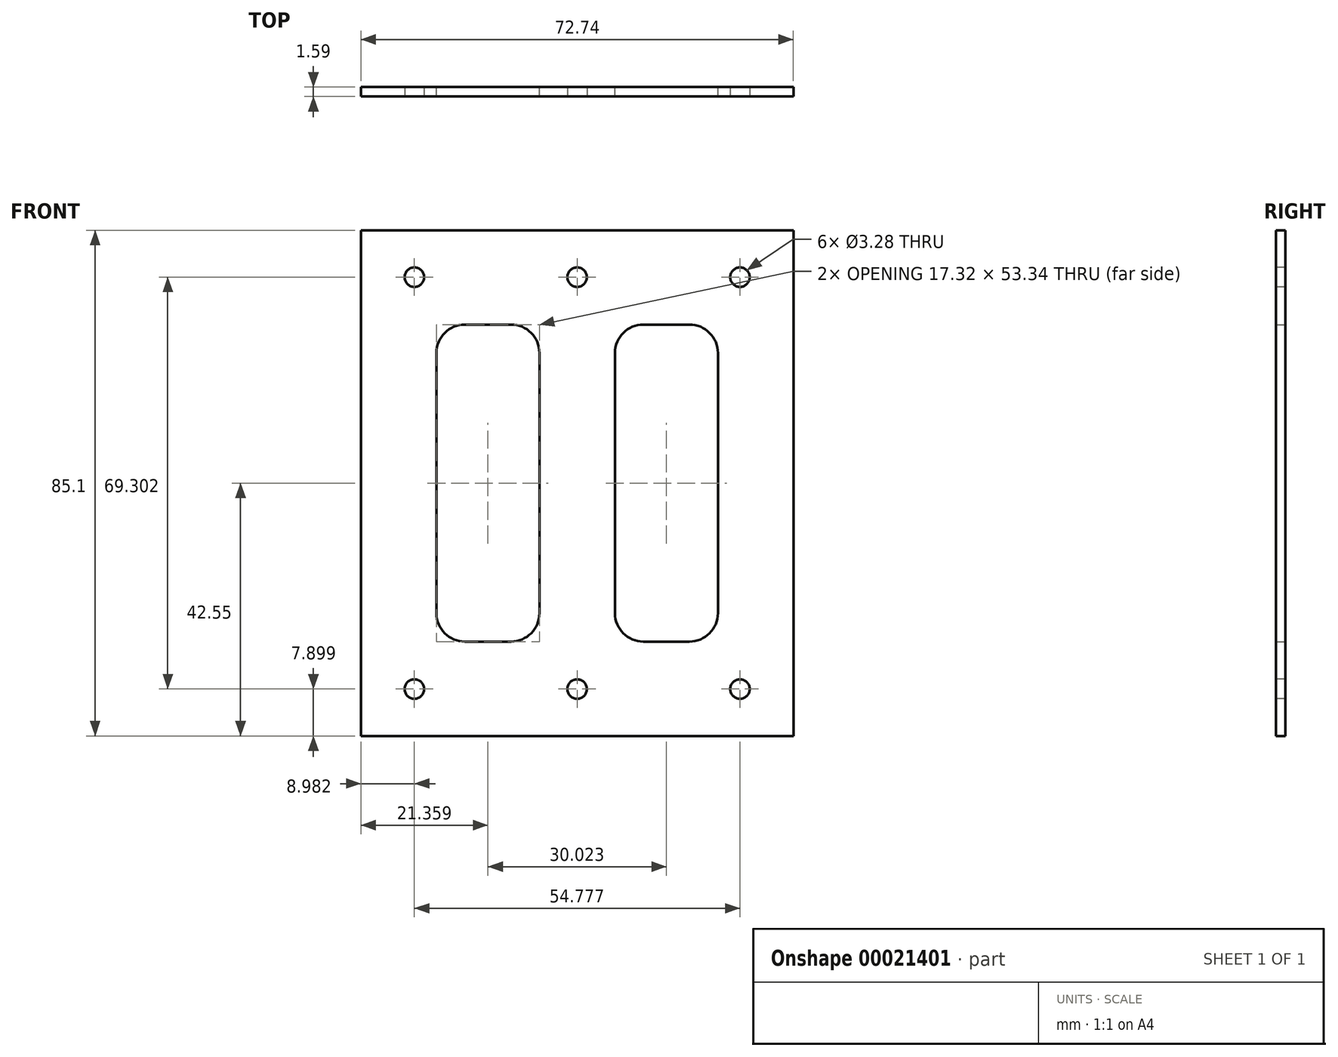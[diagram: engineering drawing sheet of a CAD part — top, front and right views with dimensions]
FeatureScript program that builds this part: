
annotation { "Feature Type Name" : "Feature", "Feature Type Description" : "" }
export const myFeature = defineFeature(function(context is Context, id is Id, definition is map)
    precondition{}
    {
        {
            var Q0;
            Q0=qCreatedBy(makeId("Front.planeOp"),FACE);
            var sketch = newSketch(context, id + "F0", { "sketchPlane" : qUnion([Q0])});
            skLineSegment(sketch, "E0.rect.bottom", {"start": v(36.37, 42.55) * mm, "end": v(-36.37, 42.55) * mm});
            skLineSegment(sketch, "E0.rect.top", {"start": v(36.37, -42.55) * mm, "end": v(-36.37, -42.55) * mm});
            skLineSegment(sketch, "E0.rect.left", {"start": v(36.37, 42.55) * mm, "end": v(36.37, -42.55) * mm});
            skLineSegment(sketch, "E0.rect.right", {"start": v(-36.37, 42.55) * mm, "end": v(-36.37, -42.55) * mm});
            skPoint(sketch, "E0.rect.middle", {"position": v(0, 0) * mm});
            skLineSegment(sketch, "E1.bottom", {"start": v(-23.67, 26.67) * mm, "end": v(-6.35, 26.67) * mm});
            skLineSegment(sketch, "E1.top", {"start": v(-23.67, -26.67) * mm, "end": v(-6.35, -26.67) * mm});
            skLineSegment(sketch, "E1.left", {"start": v(-23.67, 26.67) * mm, "end": v(-23.67, -26.67) * mm});
            skLineSegment(sketch, "E1.right", {"start": v(-6.35, 26.67) * mm, "end": v(-6.35, -26.67) * mm});
            skLineSegment(sketch, "E2.bottom", {"start": v(6.35, -26.67) * mm, "end": v(23.67, -26.67) * mm});
            skLineSegment(sketch, "E2.top", {"start": v(6.35, 26.67) * mm, "end": v(23.67, 26.67) * mm});
            skLineSegment(sketch, "E2.left", {"start": v(6.35, -26.67) * mm, "end": v(6.35, 26.67) * mm});
            skLineSegment(sketch, "E2.right", {"start": v(23.67, -26.67) * mm, "end": v(23.67, 26.67) * mm});
            skLineSegment(sketch, "E3", {"start": v(0, 0) * mm, "end": v(0, 47.22) * mm});
            skLineSegment(sketch, "E4", {"start": v(0, 0) * mm, "end": v(48.26, 0) * mm});
            skSolve(sketch);
        }
        {
            var Q0;
            {var subQ13=sQuery(id+"F0.wireOp",EDGE,"E0.rect.top");Q0=makeQuery(id+"F0.imprint","IMPRINT",FACE,{"disambiguationData":[TD([[makeQuery(id+"F0.imprint","IMPRINT",EDGE,{"derivedFrom":subQ13}),-1.0]])]});}
            var Q1;
            {var subQ9=sQuery(id+"F0.wireOp",EDGE,"E2.top");Q1=makeQuery(id+"F0.imprint","IMPRINT",FACE,{"disambiguationData":[TD([[makeQuery(id+"F0.imprint","IMPRINT",EDGE,{"derivedFrom":subQ9}),1.0]])]});}
            extrude(context, id + "F1", {"entities" : qUnion([Q0, Q1]), "depth" : 1.59 * mm});
        }
        {
            var Q0;
            Q0=makeQuery(id+"F1.opExtrude","SWEPT_EDGE",EDGE,{"disambiguationData":[OSD([sQuery(id+"F0.wireOp",EDGE,"E2.top"),sQuery(id+"F0.wireOp",EDGE,"E2.right")])]});
            var Q1;
            Q1=makeQuery(id+"F1.opExtrude","SWEPT_EDGE",EDGE,{"disambiguationData":[OSD([sQuery(id+"F0.wireOp",EDGE,"E2.top"),sQuery(id+"F0.wireOp",EDGE,"E2.left")])]});
            var Q2;
            Q2=makeQuery(id+"F1.opExtrude","SWEPT_EDGE",EDGE,{"disambiguationData":[OSD([sQuery(id+"F0.wireOp",EDGE,"E2.bottom"),sQuery(id+"F0.wireOp",EDGE,"E2.left")])]});
            var Q3;
            Q3=makeQuery(id+"F1.opExtrude","SWEPT_EDGE",EDGE,{"disambiguationData":[OSD([sQuery(id+"F0.wireOp",EDGE,"E1.top"),sQuery(id+"F0.wireOp",EDGE,"E1.left")])]});
            var Q4;
            Q4=makeQuery(id+"F1.opExtrude","SWEPT_EDGE",EDGE,{"disambiguationData":[OSD([sQuery(id+"F0.wireOp",EDGE,"E1.top"),sQuery(id+"F0.wireOp",EDGE,"E1.right")])]});
            var Q5;
            Q5=makeQuery(id+"F1.opExtrude","SWEPT_EDGE",EDGE,{"disambiguationData":[OSD([sQuery(id+"F0.wireOp",EDGE,"E1.bottom"),sQuery(id+"F0.wireOp",EDGE,"E1.left")])]});
            var Q6;
            Q6=makeQuery(id+"F1.opExtrude","SWEPT_EDGE",EDGE,{"disambiguationData":[OSD([sQuery(id+"F0.wireOp",EDGE,"E1.bottom"),sQuery(id+"F0.wireOp",EDGE,"E1.right")])]});
            var Q7;
            Q7=makeQuery(id+"F1.opExtrude","SWEPT_EDGE",EDGE,{"disambiguationData":[OSD([sQuery(id+"F0.wireOp",EDGE,"E2.bottom"),sQuery(id+"F0.wireOp",EDGE,"E2.right")])]});
            fillet(context, id + "F2", {"entities" : qUnion([Q0, Q1, Q2, Q3, Q4, Q5, Q6, Q7]), "radius" : 4.78 * mm, "tangentPropagation" : true, "allowEdgeOverflow" : false});
        }
        {
            var Q0;
            Q0=makeQuery(id+"F1.opExtrude","CAP_FACE",FACE,{"disambiguationData":[OSD([sQuery(id+"F0.wireOp",EDGE,"E0.rect.bottom"),sQuery(id+"F0.wireOp",EDGE,"E0.rect.top"),sQuery(id+"F0.wireOp",EDGE,"E0.rect.left"),sQuery(id+"F0.wireOp",EDGE,"E0.rect.right"),sQuery(id+"F0.wireOp",EDGE,"E1.bottom"),sQuery(id+"F0.wireOp",EDGE,"E1.top"),sQuery(id+"F0.wireOp",EDGE,"E1.left"),sQuery(id+"F0.wireOp",EDGE,"E1.right"),sQuery(id+"F0.wireOp",EDGE,"E2.bottom"),sQuery(id+"F0.wireOp",EDGE,"E2.top"),sQuery(id+"F0.wireOp",EDGE,"E2.left"),sQuery(id+"F0.wireOp",EDGE,"E2.right")])],"isStart":false});
            var sketch = newSketch(context, id + "F3", { "sketchPlane" : qUnion([Q0])});
            skLineSegment(sketch, "E5.rect.bottom", {"start": v(27.39, -34.65) * mm, "end": v(-27.39, -34.65) * mm});
            skLineSegment(sketch, "E5.rect.top", {"start": v(27.39, 34.65) * mm, "end": v(-27.39, 34.65) * mm});
            skLineSegment(sketch, "E5.rect.left", {"start": v(27.39, -34.65) * mm, "end": v(27.39, 34.65) * mm});
            skLineSegment(sketch, "E5.rect.right", {"start": v(-27.39, -34.65) * mm, "end": v(-27.39, 34.65) * mm});
            skPoint(sketch, "E5.rect.middle", {"position": v(0, 0) * mm});
            skLineSegment(sketch, "E6", {"start": v(0, 34.65) * mm, "end": v(0, -34.65) * mm});
            skSolve(sketch);
        }
        {
            var Q0;
            Q0=sQuery(id+"F3.wireOp",VERTEX,"E5.rect.right.end");
            var Q1;
            Q1=sQuery(id+"F3.wireOp",VERTEX,"E6.start");
            var Q2;
            Q2=sQuery(id+"F3.wireOp",VERTEX,"E5.rect.left.end");
            var Q3;
            Q3=sQuery(id+"F3.wireOp",VERTEX,"E5.rect.right.start");
            var Q4;
            Q4=sQuery(id+"F3.wireOp",VERTEX,"E6.end");
            var Q5;
            Q5=sQuery(id+"F3.wireOp",VERTEX,"E5.rect.bottom.start");
            var Q6;
            Q6=makeQuery(id+"F1.opExtrude","SWEPT_BODY",BODY,{"disambiguationData":[OSD([sQuery(id+"F0.wireOp",EDGE,"E0.rect.bottom"),sQuery(id+"F0.wireOp",EDGE,"E0.rect.top"),sQuery(id+"F0.wireOp",EDGE,"E0.rect.left"),sQuery(id+"F0.wireOp",EDGE,"E0.rect.right"),sQuery(id+"F0.wireOp",EDGE,"E1.bottom"),sQuery(id+"F0.wireOp",EDGE,"E1.top"),sQuery(id+"F0.wireOp",EDGE,"E1.left"),sQuery(id+"F0.wireOp",EDGE,"E1.right"),sQuery(id+"F0.wireOp",EDGE,"E2.bottom"),sQuery(id+"F0.wireOp",EDGE,"E2.top"),sQuery(id+"F0.wireOp",EDGE,"E2.left"),sQuery(id+"F0.wireOp",EDGE,"E2.right")])]});
            hole(context, id + "F4", {"style" : HoleStyle.SIMPLE, "holeDiameter" : 3.28 * mm, "endStyle" : HoleEndStyle.THROUGH, "locations" : qUnion([Q0, Q1, Q2, Q3, Q4, Q5]), "scope" : qUnion([Q6])});
        }
    });
